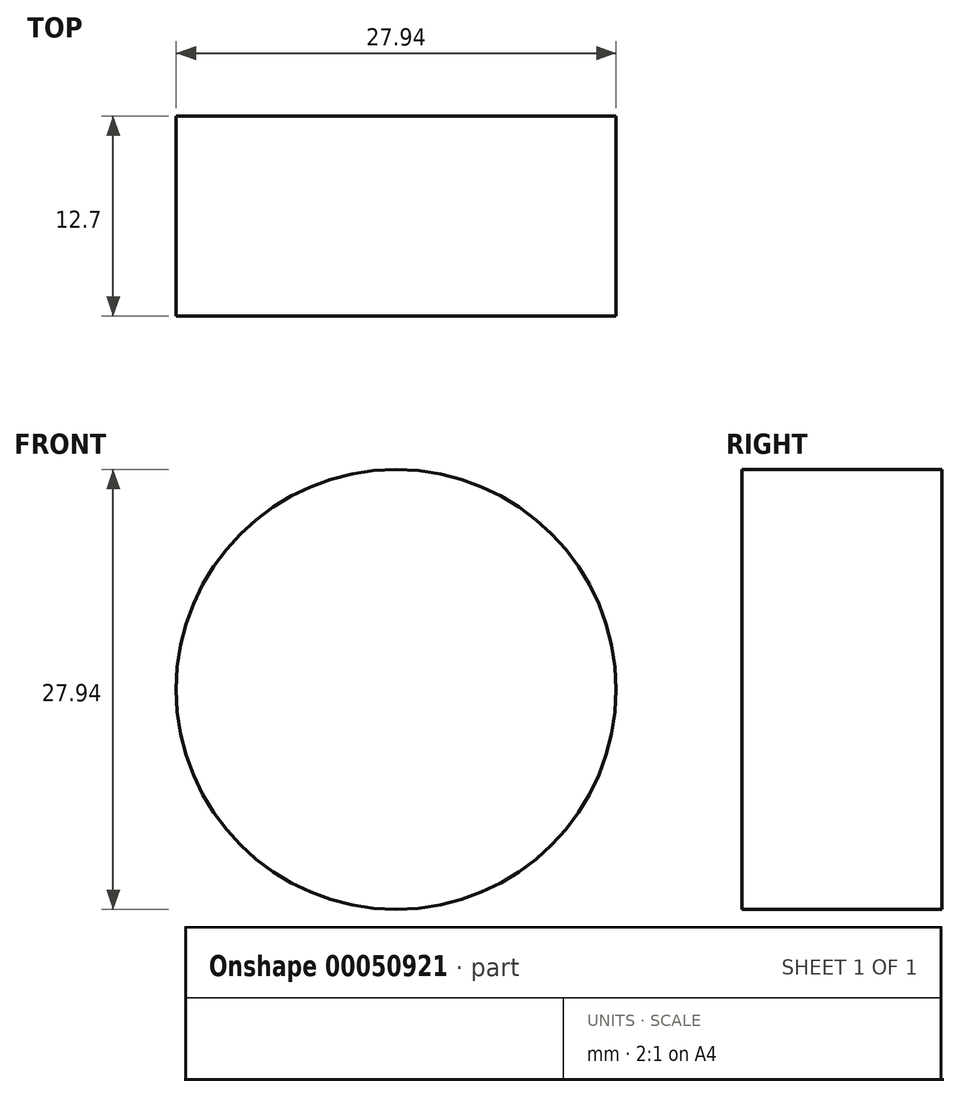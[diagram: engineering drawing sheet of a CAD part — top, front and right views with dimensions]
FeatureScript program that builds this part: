
annotation { "Feature Type Name" : "Feature", "Feature Type Description" : "" }
export const myFeature = defineFeature(function(context is Context, id is Id, definition is map)
    precondition{}
    {
        {
            var Q0;
            Q0=qCreatedBy(makeId("Front.planeOp"),FACE);
            var sketch = newSketch(context, id + "F0", { "sketchPlane" : qUnion([Q0])});
            skCircle(sketch, "E0", {"center": v(0, 0) * mm, "radius": 13.97 * mm});
            skSolve(sketch);
        }
        {
            var Q0;
            Q0=makeQuery(id+"F0.imprint","IMPRINT",FACE,{"disambiguationData":[TD([[makeQuery(id+"F0.imprint","IMPRINT",EDGE,{"derivedFrom":sQuery(id+"F0.wireOp",EDGE,"E0")}),1.0]])]});
            extrude(context, id + "F1", {"entities" : qUnion([Q0]), "depth" : 12.7 * mm});
        }
    });
